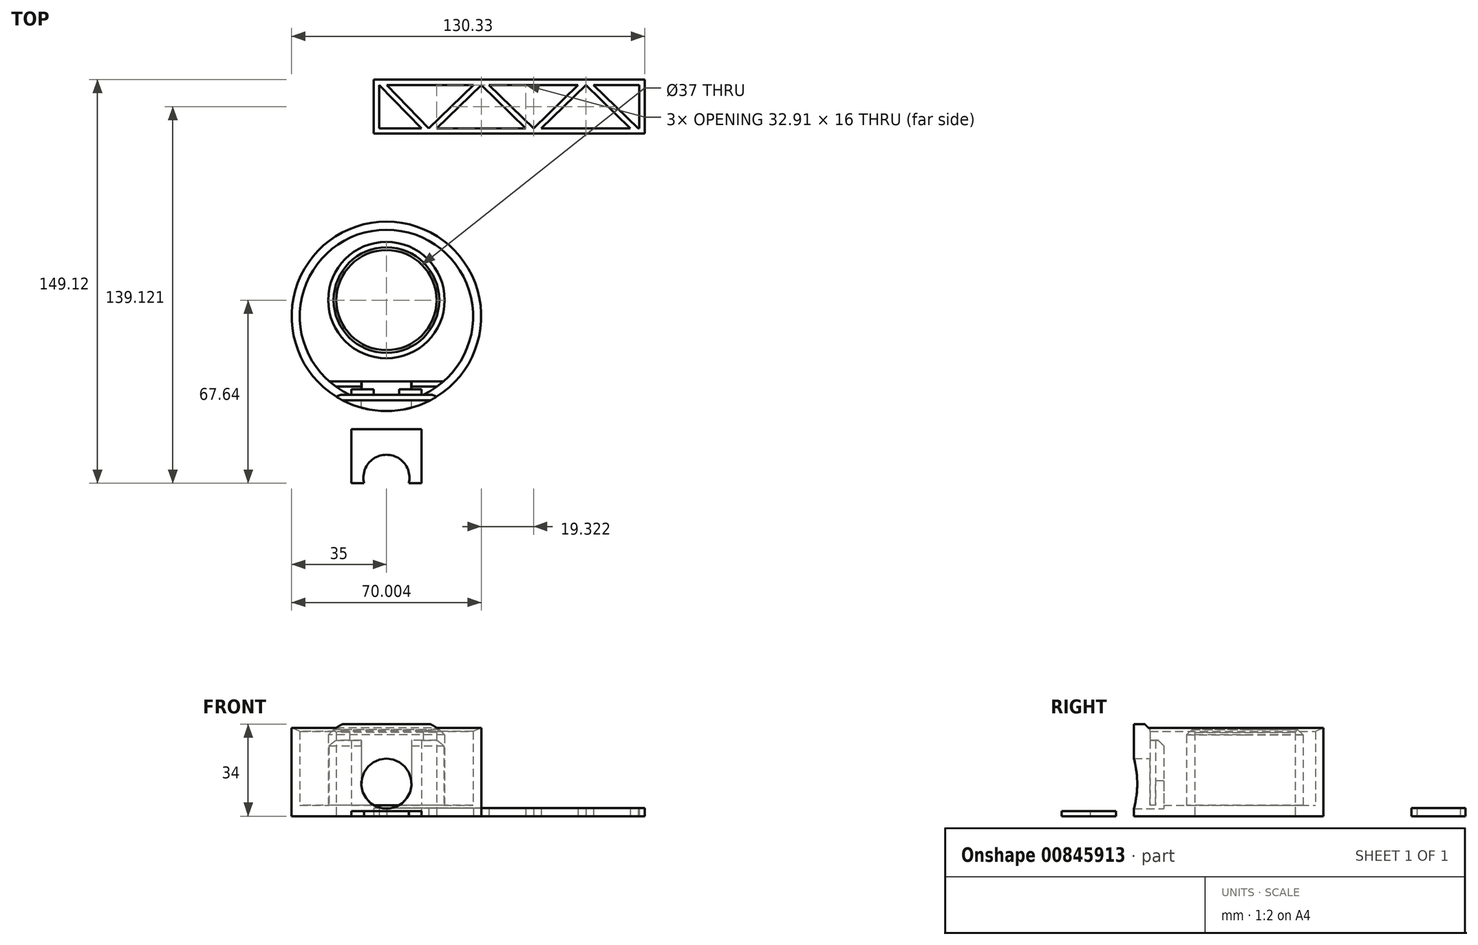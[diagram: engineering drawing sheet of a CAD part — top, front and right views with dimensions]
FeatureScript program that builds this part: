
annotation { "Feature Type Name" : "Feature", "Feature Type Description" : "" }
export const myFeature = defineFeature(function(context is Context, id is Id, definition is map)
    precondition{}
    {
        {
            var Q0;
            Q0=qCreatedBy(makeId("Top.planeOp"),FACE);
            var sketch = newSketch(context, id + "F0", { "sketchPlane" : qUnion([Q0])});
            skCircle(sketch, "E0", {"center": v(0, 0) * mm, "radius": 35 * mm});
            skLineSegment(sketch, "E1", {"start": v(-4.67, 67.48) * mm, "end": v(95.33, 67.48) * mm});
            skLineSegment(sketch, "E2", {"start": v(95.33, 67.48) * mm, "end": v(95.33, 87.48) * mm});
            skLineSegment(sketch, "E3", {"start": v(95.33, 87.48) * mm, "end": v(-4.67, 87.48) * mm});
            skLineSegment(sketch, "E4", {"start": v(-4.67, 87.48) * mm, "end": v(-4.67, 67.48) * mm});
            skLineSegment(sketch, "E5", {"start": v(-2.67, 85.48) * mm, "end": v(-2.67, 69.48) * mm});
            skLineSegment(sketch, "E6", {"start": v(-2.67, 69.48) * mm, "end": v(93.33, 69.48) * mm});
            skLineSegment(sketch, "E7", {"start": v(93.33, 69.48) * mm, "end": v(93.33, 85.48) * mm});
            skLineSegment(sketch, "E8", {"start": v(93.33, 85.48) * mm, "end": v(-2.67, 85.48) * mm});
            skLineSegment(sketch, "E9", {"start": v(-2.67, 85.48) * mm, "end": v(12.9, 69.48) * mm});
            skLineSegment(sketch, "E10", {"start": v(0, 85.6) * mm, "end": v(15.68, 69.48) * mm});
            skLineSegment(sketch, "E11", {"start": v(15.68, 69.48) * mm, "end": v(32.14, 85.48) * mm});
            skLineSegment(sketch, "E12", {"start": v(18.55, 69.48) * mm, "end": v(35, 85.48) * mm});
            skLineSegment(sketch, "E13", {"start": v(35, 85.48) * mm, "end": v(51.46, 69.48) * mm});
            skLineSegment(sketch, "E14", {"start": v(37.87, 85.48) * mm, "end": v(54.33, 69.48) * mm});
            skLineSegment(sketch, "E15", {"start": v(54.33, 69.48) * mm, "end": v(70.78, 85.48) * mm});
            skLineSegment(sketch, "E16", {"start": v(57.2, 69.48) * mm, "end": v(73.65, 85.48) * mm});
            skLineSegment(sketch, "E17", {"start": v(73.65, 85.48) * mm, "end": v(90.1, 69.48) * mm});
            skLineSegment(sketch, "E18", {"start": v(76.52, 85.48) * mm, "end": v(92.97, 69.48) * mm});
            skLineSegment(sketch, "E19", {"start": v(-13, -41.64) * mm, "end": v(0, -41.64) * mm});
            skLineSegment(sketch, "E20", {"start": v(-13, -41.64) * mm, "end": v(-13, -61.64) * mm});
            skPoint(sketch, "E21", {"position": v(0, -59.64) * mm});
            skLineSegment(sketch, "E22", {"start": v(-13, -61.64) * mm, "end": v(0, -61.64) * mm});
            skArc(sketch, "E23", {"start": v(0, -51.14) * mm, "mid": v(-6.68, -54.39) * mm, "end": v(-8.26, -61.64) * mm});
            skLineSegment(sketch, "E24", {"start": v(0, -36.93) * mm, "end": v(0, -42.73) * mm});
            skLineSegment(sketch, "E25.MirrorCS", {"start": v(13, -41.64) * mm, "end": v(0, -41.64) * mm});
            skLineSegment(sketch, "E26.MirrorCS", {"start": v(13, -61.64) * mm, "end": v(0, -61.64) * mm});
            skLineSegment(sketch, "E27.MirrorCS", {"start": v(13, -41.64) * mm, "end": v(13, -61.64) * mm});
            skArc(sketch, "E28.MirrorCS", {"start": v(0, -51.14) * mm, "mid": v(6.68, -54.39) * mm, "end": v(8.26, -61.64) * mm});
            skSolve(sketch);
        }
        {
            var Q0;
            Q0=makeQuery(id+"F0.imprint","IMPRINT",FACE,{"disambiguationData":[TD([[makeQuery(id+"F0.imprint","IMPRINT",EDGE,{"derivedFrom":sQuery(id+"F0.wireOp",EDGE,"E0")}),1.0]])]});
            extrude(context, id + "F1", {"entities" : qUnion([Q0]), "depth" : 4 * mm, "offsetDistance" : 25 * mm});
        }
        {
            var Q0;
            Q0=makeQuery(id+"F1.opExtrude","CAP_FACE",FACE,{"disambiguationData":[OSD([sQuery(id+"F0.wireOp",EDGE,"E0")])],"isStart":false});
            var sketch = newSketch(context, id + "F2", { "sketchPlane" : qUnion([Q0])});
            skLineSegment(sketch, "E29", {"start": v(-19.6, -29) * mm, "end": v(19.6, -29) * mm});
            skArc(sketch, "E30", {"start": v(-19.6, -29) * mm, "mid": v(0, 35) * mm, "end": v(19.6, -29) * mm});
            skArc(sketch, "E31", {"start": v(-13.53, -29) * mm, "mid": v(0, 32) * mm, "end": v(13.53, -29) * mm});
            skPoint(sketch, "E32", {"position": v(0, 6) * mm});
            skCircle(sketch, "E33", {"center": v(0, 6) * mm, "radius": 21.5 * mm});
            skCircle(sketch, "E34", {"center": v(0, 6) * mm, "radius": 18.5 * mm});
            skLineSegment(sketch, "E35", {"start": v(-13, -29) * mm, "end": v(-13, -27) * mm});
            skLineSegment(sketch, "E36", {"start": v(-13, -27) * mm, "end": v(-9.25, -27) * mm});
            skLineSegment(sketch, "E37", {"start": v(-9.25, -27) * mm, "end": v(-9.25, -24) * mm});
            skLineSegment(sketch, "E38", {"start": v(-9.25, -24) * mm, "end": v(-21.17, -24) * mm});
            skLineSegment(sketch, "E39", {"start": v(0, 6) * mm, "end": v(0, -7.52) * mm});
            skLineSegment(sketch, "E40.MirrorCS", {"start": v(13, -29) * mm, "end": v(13, -27) * mm});
            skLineSegment(sketch, "E41.MirrorCS", {"start": v(13, -27) * mm, "end": v(9.25, -27) * mm});
            skLineSegment(sketch, "E42.MirrorCS", {"start": v(9.25, -24) * mm, "end": v(21.17, -24) * mm});
            skLineSegment(sketch, "E43.MirrorCS", {"start": v(9.25, -27) * mm, "end": v(9.25, -24) * mm});
            skLineSegment(sketch, "E44", {"start": v(-9.25, -27) * mm, "end": v(9.25, -27) * mm});
            skLineSegment(sketch, "E45", {"start": v(-9.25, -24) * mm, "end": v(9.25, -24) * mm});
            skSolve(sketch);
        }
        {
            var Q0;
            {var subQ0=sQuery(id+"F2.wireOp",EDGE,"E30");Q0=makeQuery(id+"F2.imprint","IMPRINT",FACE,{"disambiguationData":[TD([[makeQuery(id+"F2.imprint","IMPRINT",EDGE,{"derivedFrom":subQ0}),1.0]])]});}
            var Q1;
            {var subQ1=sQuery(id+"F2.wireOp",EDGE,"E29");var subQ4=sQuery(id+"F2.wireOp",EDGE,"E31");var subQ5=makeQuery(id+"F2.imprint","INTERSECT",VERTEX,{"disambiguationData":[OD(0.0)],"derivedFrom":[subQ1,subQ4]});Q1=makeQuery(id+"F2.imprint","IMPRINT",FACE,{"disambiguationData":[TD([[makeQuery(id+"F2.imprint","IMPRINT",EDGE,{"disambiguationData":[TD([[subQ5,-1.0]])],"derivedFrom":subQ1}),-1.0]])]});}
            extrude(context, id + "F3", {"entities" : qUnion([Q0, Q1]), "operationType" : NewBodyOperationType.ADD, "depth" : 30 * mm, "offsetDistance" : 25 * mm});
        }
        {
            var Q0;
            Q0=makeQuery(id+"F2.imprint","IMPRINT",FACE,{"disambiguationData":[TD([[makeQuery(id+"F2.imprint","IMPRINT",EDGE,{"derivedFrom":sQuery(id+"F2.wireOp",EDGE,"E33")}),1.0]])]});
            extrude(context, id + "F4", {"entities" : qUnion([Q0]), "operationType" : NewBodyOperationType.ADD, "depth" : 28 * mm, "offsetDistance" : 25 * mm});
        }
        {
            var Q0;
            Q0=makeQuery(id+"F3.opExtrude","CAP_EDGE",EDGE,{"disambiguationData":[OSD([sQuery(id+"F2.wireOp",EDGE,"E31")])],"isStart":false});
            chamfer(context, id + "F5", {"entities" : qUnion([Q0]), "chamferType" : ChamferType.TWO_OFFSETS, "width1" : 2.7 * mm, "oppositeDirection" : false, "width2" : 6 * mm, "tangentPropagation" : true});
        }
        {
            var Q0;
            Q0=makeQuery(id+"F4.opExtrude","CAP_EDGE",EDGE,{"disambiguationData":[OSD([sQuery(id+"F2.wireOp",EDGE,"E34")])],"isStart":false});
            chamfer(context, id + "F6", {"entities" : qUnion([Q0]), "width" : 1 * mm, "tangentPropagation" : true});
        }
        {
            var Q0;
            Q0=sQuery(id+"F2.wireOp",VERTEX,"E32");
            var Q1;
            Q1=makeQuery(id+"F1.opExtrude","SWEPT_BODY",BODY,{"disambiguationData":[OSD([sQuery(id+"F0.wireOp",EDGE,"E0")])]});
            hole(context, id + "F7", {"style" : HoleStyle.SIMPLE, "endStyle" : HoleEndStyle.THROUGH, "holeDiameter" : 37 * mm, "majorDiameter" : 5 * mm, "isTappedThrough" : true, "tappedDepth" : 12 * mm, "tapClearance" : 3, "locations" : qUnion([Q0]), "scope" : qUnion([Q1])});
        }
        {
            var Q0;
            Q0=makeQuery(id+"F3.opExtrude","SWEPT_FACE",FACE,{"disambiguationData":[OSD([sQuery(id+"F2.wireOp",EDGE,"E29")])]});
            var sketch = newSketch(context, id + "F8", { "sketchPlane" : qUnion([Q0])});
            skPoint(sketch, "E46", {"position": v(0, 12) * mm});
            skPoint(sketch, "E46.positionSnap0", {"position": v(0, 4) * mm});
            skCircle(sketch, "E47", {"center": v(0, 12) * mm, "radius": 9.25 * mm});
            skLineSegment(sketch, "E48", {"start": v(-4.64, 4) * mm, "end": v(4.64, 4) * mm});
            skCircle(sketch, "E49.cCircle", {"center": v(0, 12) * mm, "radius": 13.5 * mm, "construction": true});
            skLineSegment(sketch, "E49.0", {"start": v(-15.59, 11.93) * mm, "end": v(-7.85, 25.47) * mm});
            skLineSegment(sketch, "E49.1", {"start": v(-7.85, 25.47) * mm, "end": v(7.74, 25.53) * mm});
            skLineSegment(sketch, "E49.2", {"start": v(7.74, 25.53) * mm, "end": v(15.59, 12.07) * mm});
            skLineSegment(sketch, "E49.3", {"start": v(15.59, 12.07) * mm, "end": v(7.85, -1.47) * mm});
            skLineSegment(sketch, "E49.4", {"start": v(7.85, -1.47) * mm, "end": v(-7.74, -1.53) * mm});
            skLineSegment(sketch, "E49.5", {"start": v(-7.74, -1.53) * mm, "end": v(-15.59, 11.93) * mm});
            skPoint(sketch, "E49.0.midPoint", {"position": v(-11.72, 18.7) * mm});
            skCircle(sketch, "E50", {"center": v(0, 12) * mm, "radius": 14.5 * mm});
            skSolve(sketch);
        }
        {
            var Q0;
            Q0=sQuery(id+"F8.wireOp",VERTEX,"E46");
            var Q1;
            Q1=makeQuery(id+"F1.opExtrude","SWEPT_BODY",BODY,{"disambiguationData":[OSD([sQuery(id+"F0.wireOp",EDGE,"E0")])]});
            hole(context, id + "F9", {"style" : HoleStyle.SIMPLE, "endStyle" : HoleEndStyle.THROUGH, "holeDiameter" : 18.5 * mm, "majorDiameter" : 5 * mm, "isTappedThrough" : true, "tappedDepth" : 12 * mm, "tapClearance" : 3, "locations" : qUnion([Q0]), "scope" : qUnion([Q1])});
        }
        {
            var Q0;
            Q0=makeQuery(id+"F0.imprint","IMPRINT",FACE,{"disambiguationData":[TD([[makeQuery(id+"F0.imprint","IMPRINT",EDGE,{"derivedFrom":sQuery(id+"F0.wireOp",EDGE,"E1")}),1.0]])]});
            var Q1;
            {var subQ0=sQuery(id+"F0.wireOp",EDGE,"E9");Q1=makeQuery(id+"F0.imprint","IMPRINT",FACE,{"disambiguationData":[TD([[makeQuery(id+"F0.imprint","IMPRINT",EDGE,{"derivedFrom":subQ0}),1.0]])]});}
            var Q2;
            {var subQ0=sQuery(id+"F0.wireOp",EDGE,"ZEzCryKx-d35V-rLPh-8Ipi-TqEoNOP6QNBv");Q2=makeQuery(id+"F0.imprint","IMPRINT",FACE,{"disambiguationData":[TD([[makeQuery(id+"F0.imprint","IMPRINT",EDGE,{"derivedFrom":subQ0}),-1.0]])]});}
            var Q3;
            {var subQ0=sQuery(id+"F0.wireOp",EDGE,"CKcMsAwK-7OZE-CR44-AOlV-Set6mfz6AY0q");Q3=makeQuery(id+"F0.imprint","IMPRINT",FACE,{"disambiguationData":[TD([[makeQuery(id+"F0.imprint","IMPRINT",EDGE,{"derivedFrom":subQ0}),1.0]])]});}
            var Q4;
            {var subQ0=sQuery(id+"F0.wireOp",EDGE,"r0q0Udh3-En3A-4cJC-71GK-qILipopqXV0B");Q4=makeQuery(id+"F0.imprint","IMPRINT",FACE,{"disambiguationData":[TD([[makeQuery(id+"F0.imprint","IMPRINT",EDGE,{"derivedFrom":subQ0}),-1.0]])]});}
            var Q5;
            {var subQ2=sQuery(id+"F0.wireOp",EDGE,"RvI4HVYa-QjRP-7Kfp-bFOd-DoB1SwzRbHW2");Q5=makeQuery(id+"F0.imprint","IMPRINT",FACE,{"disambiguationData":[TD([[makeQuery(id+"F0.imprint","IMPRINT",EDGE,{"derivedFrom":subQ2}),1.0]])]});}
            var Q6;
            {var subQ0=sQuery(id+"F0.wireOp",EDGE,"E11");Q6=makeQuery(id+"F0.imprint","IMPRINT",FACE,{"disambiguationData":[TD([[makeQuery(id+"F0.imprint","IMPRINT",EDGE,{"derivedFrom":subQ0}),-1.0]])]});}
            var Q7;
            {var subQ0=sQuery(id+"F0.wireOp",EDGE,"E13");Q7=makeQuery(id+"F0.imprint","IMPRINT",FACE,{"disambiguationData":[TD([[makeQuery(id+"F0.imprint","IMPRINT",EDGE,{"derivedFrom":subQ0}),1.0]])]});}
            var Q8;
            {var subQ0=sQuery(id+"F0.wireOp",EDGE,"E15");Q8=makeQuery(id+"F0.imprint","IMPRINT",FACE,{"disambiguationData":[TD([[makeQuery(id+"F0.imprint","IMPRINT",EDGE,{"derivedFrom":subQ0}),-1.0]])]});}
            var Q9;
            {var subQ0=sQuery(id+"F0.wireOp",EDGE,"E17");Q9=makeQuery(id+"F0.imprint","IMPRINT",FACE,{"disambiguationData":[TD([[makeQuery(id+"F0.imprint","IMPRINT",EDGE,{"derivedFrom":subQ0}),1.0]])]});}
            extrude(context, id + "F10", {"entities" : qUnion([Q0, Q1, Q2, Q3, Q4, Q5, Q6, Q7, Q8, Q9]), "depth" : 3 * mm, "offsetDistance" : 25 * mm});
        }
        {
            var Q0;
            {var subQ0=sQuery(id+"F2.wireOp",EDGE,"E35");Q0=makeQuery(id+"F2.imprint","IMPRINT",FACE,{"disambiguationData":[TD([[makeQuery(id+"F2.imprint","IMPRINT",EDGE,{"derivedFrom":subQ0}),1.0]])]});}
            var Q1;
            {var subQ0=sQuery(id+"F2.wireOp",EDGE,"E40.MirrorCS");Q1=makeQuery(id+"F2.imprint","IMPRINT",FACE,{"disambiguationData":[TD([[makeQuery(id+"F2.imprint","IMPRINT",EDGE,{"derivedFrom":subQ0}),-1.0]])]});}
            extrude(context, id + "F11", {"entities" : qUnion([Q0, Q1]), "operationType" : NewBodyOperationType.ADD, "depth" : 24 * mm, "offsetDistance" : 25 * mm});
        }
        {
            var Q0;
            Q0=makeQuery(id+"F2.imprint","IMPRINT",FACE,{"disambiguationData":[TD([[makeQuery(id+"F2.imprint","IMPRINT",EDGE,{"derivedFrom":sQuery(id+"F2.wireOp",EDGE,"E37")}),-1.0]])]});
            extrude(context, id + "F12", {"entities" : qUnion([Q0]), "operationType" : NewBodyOperationType.ADD, "depth" : 9 * mm, "offsetDistance" : 25 * mm});
        }
        {
            var Q0;
            {var subQ0=sQuery(id+"F8.wireOp",EDGE,"E48");Q0=makeQuery(id+"F8.imprint","IMPRINT",FACE,{"disambiguationData":[TD([[makeQuery(id+"F8.imprint","IMPRINT",EDGE,{"derivedFrom":subQ0}),-1.0]])]});}
            var Q1;
            {var subQ0=sQuery(id+"F8.wireOp",EDGE,"E48");Q1=makeQuery(id+"F8.imprint","IMPRINT",FACE,{"disambiguationData":[TD([[makeQuery(id+"F8.imprint","IMPRINT",EDGE,{"derivedFrom":subQ0}),1.0]])]});}
            extrude(context, id + "F13", {"entities" : qUnion([Q0, Q1]), "operationType" : NewBodyOperationType.REMOVE, "depth" : 5 * mm, "offsetDistance" : 25 * mm});
        }
        {
            var Q0;
            Q0=makeQuery(id+"F0.imprint","IMPRINT",FACE,{"disambiguationData":[TD([[makeQuery(id+"F0.imprint","IMPRINT",EDGE,{"derivedFrom":sQuery(id+"F0.wireOp",EDGE,"E19")}),-1.0]])]});
            extrude(context, id + "F14", {"entities" : qUnion([Q0]), "depth" : 1.9 * mm, "offsetDistance" : 25 * mm});
        }
        {
            var Q0;
            Q0=makeQuery(id+"F4.opExtrude","CAP_EDGE",EDGE,{"disambiguationData":[OSD([sQuery(id+"F2.wireOp",EDGE,"E33")])],"isStart":false});
            chamfer(context, id + "F15", {"entities" : qUnion([Q0]), "width" : 2 * mm, "tangentPropagation" : true});
        }
        {
            var Q0;
            Q0=makeQuery(id+"F11.opExtrude","CAP_EDGE",EDGE,{"disambiguationData":[OSD([sQuery(id+"F2.wireOp",EDGE,"E38")])],"isStart":false});
            var Q1;
            Q1=makeQuery(id+"F11.opExtrude","CAP_EDGE",EDGE,{"disambiguationData":[OSD([sQuery(id+"F2.wireOp",EDGE,"E42.MirrorCS")])],"isStart":false});
            var Q2;
            Q2=makeQuery(id+"F3.opExtrude","CAP_EDGE",EDGE,{"disambiguationData":[OSD([sQuery(id+"F2.wireOp",EDGE,"E29")])],"isStart":false});
            chamfer(context, id + "F16", {"entities" : qUnion([Q0, Q1, Q2]), "width" : 2 * mm, "tangentPropagation" : true});
        }
    });
